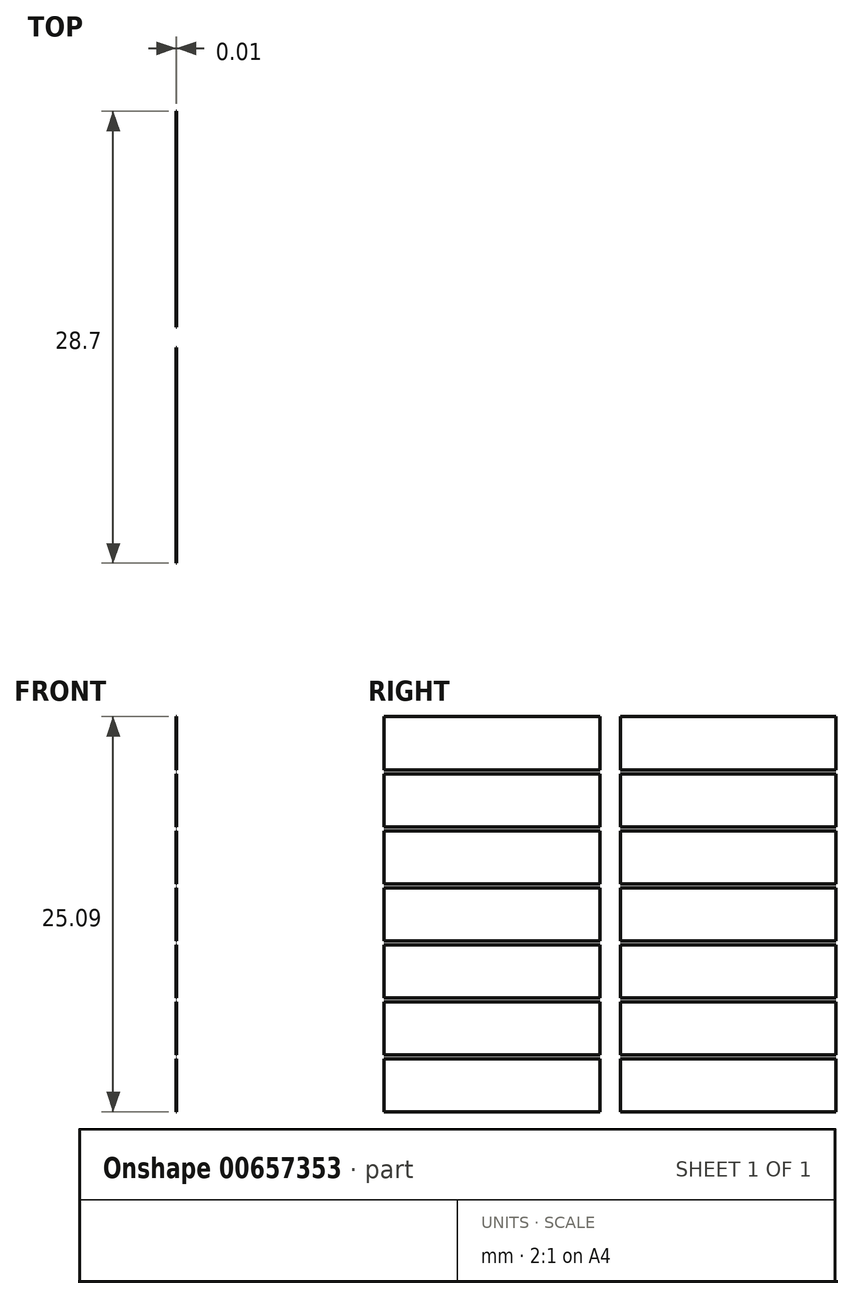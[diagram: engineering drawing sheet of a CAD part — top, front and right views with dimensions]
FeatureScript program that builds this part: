
annotation { "Feature Type Name" : "Feature", "Feature Type Description" : "" }
export const myFeature = defineFeature(function(context is Context, id is Id, definition is map)
    precondition{}
    {
        {
            var Q0;
            Q0=qCreatedBy(makeId("Right.planeOp"),FACE);
            var sketch = newSketch(context, id + "F0", { "sketchPlane" : qUnion([Q0])});
            skPoint(sketch, "E0.0", {"position": v(0, 0) * mm});
            skLineSegment(sketch, "E1.bottom", {"start": v(0, 0) * mm, "end": v(30, 0) * mm});
            skLineSegment(sketch, "E1.top", {"start": v(0, -30) * mm, "end": v(30, -30) * mm});
            skLineSegment(sketch, "E1.left", {"start": v(0, 0) * mm, "end": v(0, -30) * mm});
            skLineSegment(sketch, "E1.right", {"start": v(30, 0) * mm, "end": v(30, -30) * mm});
            skLineSegment(sketch, "E2.1", {"start": v(0.65, -0.65) * mm, "end": v(14.35, -0.65) * mm});
            skLineSegment(sketch, "E2.2", {"start": v(0.65, -0.65) * mm, "end": v(0.65, -2.2) * mm});
            skLineSegment(sketch, "E3", {"start": v(14.35, -2.2) * mm, "end": v(14.35, -0.65) * mm});
            skPoint(sketch, "E4.MirrorP", {"position": v(11.5, 0) * mm});
            skPoint(sketch, "E5.orphan", {"position": v(0, -26.74) * mm});
            skLineSegment(sketch, "E6", {"start": v(0.65, -2.46) * mm, "end": v(0.65, -4.02) * mm});
            skLineSegment(sketch, "E7", {"start": v(0.65, -4.02) * mm, "end": v(14.35, -4.02) * mm});
            skLineSegment(sketch, "E8", {"start": v(14.35, -4.02) * mm, "end": v(14.35, -2.46) * mm});
            skLineSegment(sketch, "E9.0", {"start": v(0.65, -4.27) * mm, "end": v(14.35, -4.27) * mm});
            skLineSegment(sketch, "E10", {"start": v(0.65, -4.27) * mm, "end": v(0.65, -5.83) * mm});
            skLineSegment(sketch, "E11", {"start": v(14.35, -5.83) * mm, "end": v(14.35, -4.27) * mm});
            skLineSegment(sketch, "E12.0", {"start": v(0.65, -7.64) * mm, "end": v(14.35, -7.64) * mm});
            skLineSegment(sketch, "E13", {"start": v(0.65, -6.08) * mm, "end": v(0.65, -7.64) * mm});
            skLineSegment(sketch, "E14", {"start": v(14.35, -6.08) * mm, "end": v(14.35, -7.64) * mm});
            skLineSegment(sketch, "E15.0", {"start": v(0.65, -7.9) * mm, "end": v(14.35, -7.9) * mm});
            skLineSegment(sketch, "E16", {"start": v(0.65, -7.9) * mm, "end": v(0.65, -9.45) * mm});
            skLineSegment(sketch, "E17", {"start": v(14.35, -9.45) * mm, "end": v(14.35, -7.9) * mm});
            skLineSegment(sketch, "E18.0", {"start": v(0.65, -11.26) * mm, "end": v(14.35, -11.26) * mm});
            skLineSegment(sketch, "E19", {"start": v(0.65, -9.7) * mm, "end": v(0.65, -11.26) * mm});
            skLineSegment(sketch, "E20", {"start": v(14.35, -9.7) * mm, "end": v(14.35, -11.26) * mm});
            skLineSegment(sketch, "E21.0", {"start": v(0.65, -11.51) * mm, "end": v(14.35, -11.51) * mm});
            skLineSegment(sketch, "E22", {"start": v(0.65, -11.51) * mm, "end": v(0.65, -13.07) * mm});
            skLineSegment(sketch, "E23", {"start": v(14.35, -13.07) * mm, "end": v(14.35, -11.51) * mm});
            skLineSegment(sketch, "E24.0", {"start": v(0.65, -14.88) * mm, "end": v(14.35, -14.88) * mm});
            skLineSegment(sketch, "E25", {"start": v(0.65, -13.32) * mm, "end": v(0.65, -14.88) * mm});
            skLineSegment(sketch, "E26", {"start": v(14.35, -14.88) * mm, "end": v(14.35, -13.32) * mm});
            skLineSegment(sketch, "E27.0", {"start": v(0.65, -15.13) * mm, "end": v(14.35, -15.13) * mm});
            skLineSegment(sketch, "E28", {"start": v(0.65, -15.13) * mm, "end": v(0.65, -16.7) * mm});
            skLineSegment(sketch, "E29", {"start": v(14.35, -16.7) * mm, "end": v(14.35, -15.13) * mm});
            skLineSegment(sketch, "E30.0", {"start": v(0.65, -18.5) * mm, "end": v(14.35, -18.5) * mm});
            skLineSegment(sketch, "E31", {"start": v(0.65, -16.7) * mm, "end": v(0.65, -18.5) * mm});
            skLineSegment(sketch, "E32", {"start": v(14.35, -18.5) * mm, "end": v(14.35, -16.94) * mm});
            skLineSegment(sketch, "E33.0", {"start": v(0.65, -18.75) * mm, "end": v(14.35, -18.75) * mm});
            skLineSegment(sketch, "E34", {"start": v(0.65, -18.75) * mm, "end": v(0.65, -20.31) * mm});
            skLineSegment(sketch, "E35", {"start": v(14.35, -18.75) * mm, "end": v(14.35, -20.31) * mm});
            skLineSegment(sketch, "E36.0", {"start": v(0.65, -22.12) * mm, "end": v(14.35, -22.12) * mm});
            skLineSegment(sketch, "E37", {"start": v(0.65, -20.56) * mm, "end": v(0.65, -22.12) * mm});
            skLineSegment(sketch, "E38", {"start": v(14.35, -20.56) * mm, "end": v(14.35, -22.12) * mm});
            skLineSegment(sketch, "E39.0", {"start": v(0.65, -22.37) * mm, "end": v(14.35, -22.37) * mm});
            skLineSegment(sketch, "E40", {"start": v(0.65, -22.37) * mm, "end": v(0.65, -23.93) * mm});
            skLineSegment(sketch, "E41", {"start": v(14.35, -22.37) * mm, "end": v(14.35, -23.93) * mm});
            skLineSegment(sketch, "E42.0", {"start": v(0.65, -25.74) * mm, "end": v(14.35, -25.74) * mm});
            skLineSegment(sketch, "E43", {"start": v(0.65, -24.18) * mm, "end": v(0.65, -25.74) * mm});
            skLineSegment(sketch, "E44", {"start": v(14.35, -24.18) * mm, "end": v(14.35, -25.74) * mm});
            skLineSegment(sketch, "E45", {"start": v(0.65, -2.46) * mm, "end": v(0.65, -2.2) * mm});
            skLineSegment(sketch, "E46", {"start": v(14.35, -2.46) * mm, "end": v(14.35, -2.2) * mm});
            skLineSegment(sketch, "E47", {"start": v(0.65, -6.08) * mm, "end": v(0.65, -5.83) * mm});
            skLineSegment(sketch, "E48", {"start": v(14.35, -6.08) * mm, "end": v(14.35, -5.83) * mm});
            skLineSegment(sketch, "E49", {"start": v(14.35, -24.18) * mm, "end": v(14.35, -23.93) * mm});
            skLineSegment(sketch, "E50", {"start": v(0.65, -24.18) * mm, "end": v(0.65, -23.93) * mm});
            skLineSegment(sketch, "E51", {"start": v(0.65, -20.56) * mm, "end": v(0.65, -20.31) * mm});
            skLineSegment(sketch, "E52", {"start": v(14.35, -20.56) * mm, "end": v(14.35, -20.31) * mm});
            skLineSegment(sketch, "E53", {"start": v(14.35, -16.94) * mm, "end": v(14.35, -16.7) * mm});
            skLineSegment(sketch, "E54", {"start": v(14.35, -13.32) * mm, "end": v(14.35, -13.07) * mm});
            skLineSegment(sketch, "E55", {"start": v(0.65, -13.32) * mm, "end": v(0.65, -13.07) * mm});
            skLineSegment(sketch, "E56", {"start": v(0.65, -9.7) * mm, "end": v(0.65, -9.45) * mm});
            skLineSegment(sketch, "E57", {"start": v(14.35, -9.7) * mm, "end": v(14.35, -9.45) * mm});
            skLineSegment(sketch, "E58.MirrorCS", {"start": v(29.35, -0.65) * mm, "end": v(29.35, -2.2) * mm});
            skLineSegment(sketch, "E59.MirrorCS", {"start": v(29.35, -2.46) * mm, "end": v(29.35, -2.2) * mm});
            skLineSegment(sketch, "E60.MirrorCS", {"start": v(29.35, -2.46) * mm, "end": v(29.35, -4.02) * mm});
            skLineSegment(sketch, "E61.MirrorCS", {"start": v(29.35, -20.56) * mm, "end": v(29.35, -22.12) * mm});
            skLineSegment(sketch, "E62.MirrorCS", {"start": v(15.65, -4.02) * mm, "end": v(15.65, -2.46) * mm});
            skLineSegment(sketch, "E63.MirrorCS", {"start": v(29.35, -20.56) * mm, "end": v(29.35, -20.31) * mm});
            skLineSegment(sketch, "E64.MirrorCS", {"start": v(29.35, -7.9) * mm, "end": v(29.35, -9.45) * mm});
            skLineSegment(sketch, "E65.MirrorCS", {"start": v(15.65, -16.7) * mm, "end": v(15.65, -15.13) * mm});
            skLineSegment(sketch, "E66.MirrorCS", {"start": v(29.35, -9.7) * mm, "end": v(29.35, -9.45) * mm});
            skLineSegment(sketch, "E67.MirrorCS", {"start": v(29.35, -6.08) * mm, "end": v(29.35, -5.83) * mm});
            skLineSegment(sketch, "E68.MirrorCS", {"start": v(15.65, -9.7) * mm, "end": v(15.65, -9.45) * mm});
            skLineSegment(sketch, "E69.MirrorCS", {"start": v(15.65, -22.37) * mm, "end": v(15.65, -23.93) * mm});
            skLineSegment(sketch, "E70.MirrorCS", {"start": v(29.35, -24.18) * mm, "end": v(29.35, -23.93) * mm});
            skLineSegment(sketch, "E71.MirrorCS", {"start": v(29.35, -4.27) * mm, "end": v(29.35, -5.83) * mm});
            skLineSegment(sketch, "E72.MirrorCS", {"start": v(15.65, -20.56) * mm, "end": v(15.65, -20.31) * mm});
            skLineSegment(sketch, "E73.MirrorCS", {"start": v(15.65, -9.45) * mm, "end": v(15.65, -7.9) * mm});
            skLineSegment(sketch, "E74.MirrorCS", {"start": v(29.35, -11.51) * mm, "end": v(29.35, -13.07) * mm});
            skLineSegment(sketch, "E75.MirrorCS", {"start": v(29.35, -13.32) * mm, "end": v(29.35, -13.07) * mm});
            skLineSegment(sketch, "E76.MirrorCS", {"start": v(15.65, -6.08) * mm, "end": v(15.65, -7.64) * mm});
            skLineSegment(sketch, "E77.MirrorCS", {"start": v(15.65, -14.88) * mm, "end": v(15.65, -13.32) * mm});
            skLineSegment(sketch, "E78.MirrorCS", {"start": v(29.35, -18.75) * mm, "end": v(29.35, -20.31) * mm});
            skLineSegment(sketch, "E79.MirrorCS", {"start": v(15.65, -24.18) * mm, "end": v(15.65, -23.93) * mm});
            skLineSegment(sketch, "E80.MirrorCS", {"start": v(29.35, -6.08) * mm, "end": v(29.35, -7.64) * mm});
            skLineSegment(sketch, "E81.MirrorCS", {"start": v(29.35, -13.32) * mm, "end": v(29.35, -14.88) * mm});
            skLineSegment(sketch, "E82.MirrorCS", {"start": v(15.65, -6.08) * mm, "end": v(15.65, -5.83) * mm});
            skLineSegment(sketch, "E83.MirrorCS", {"start": v(15.65, -18.5) * mm, "end": v(15.65, -16.94) * mm});
            skLineSegment(sketch, "E84.MirrorCS", {"start": v(29.35, -9.7) * mm, "end": v(29.35, -11.26) * mm});
            skLineSegment(sketch, "E85.MirrorCS", {"start": v(15.65, -13.07) * mm, "end": v(15.65, -11.51) * mm});
            skLineSegment(sketch, "E86.MirrorCS", {"start": v(15.65, -20.56) * mm, "end": v(15.65, -22.12) * mm});
            skLineSegment(sketch, "E87.MirrorCS", {"start": v(15.65, -13.32) * mm, "end": v(15.65, -13.07) * mm});
            skLineSegment(sketch, "E88.MirrorCS", {"start": v(15.65, -5.83) * mm, "end": v(15.65, -4.27) * mm});
            skLineSegment(sketch, "E89.MirrorCS", {"start": v(15.65, -9.7) * mm, "end": v(15.65, -11.26) * mm});
            skLineSegment(sketch, "E90.MirrorCS", {"start": v(29.35, -22.37) * mm, "end": v(29.35, -23.93) * mm});
            skLineSegment(sketch, "E91.MirrorCS", {"start": v(15.65, -18.75) * mm, "end": v(15.65, -20.31) * mm});
            skLineSegment(sketch, "E92.MirrorCS", {"start": v(29.35, -16.7) * mm, "end": v(29.35, -18.5) * mm});
            skLineSegment(sketch, "E93.MirrorCS", {"start": v(15.65, -2.2) * mm, "end": v(15.65, -0.65) * mm});
            skLineSegment(sketch, "E94.MirrorCS", {"start": v(29.35, -24.18) * mm, "end": v(29.35, -25.74) * mm});
            skLineSegment(sketch, "E95.MirrorCS", {"start": v(29.35, -15.13) * mm, "end": v(29.35, -16.7) * mm});
            skLineSegment(sketch, "E96.MirrorCS", {"start": v(15.65, -24.18) * mm, "end": v(15.65, -25.74) * mm});
            skLineSegment(sketch, "E97.MirrorCS", {"start": v(29.35, -4.02) * mm, "end": v(15.65, -4.02) * mm});
            skPoint(sketch, "E98.MirrorP", {"position": v(18.5, 0) * mm});
            skPoint(sketch, "E99.MirrorP", {"position": v(30, 0) * mm});
            skLineSegment(sketch, "E100.MirrorCS", {"start": v(29.35, -14.88) * mm, "end": v(15.65, -14.88) * mm});
            skLineSegment(sketch, "E101.MirrorCS", {"start": v(29.35, -0.65) * mm, "end": v(15.65, -0.65) * mm});
            skPoint(sketch, "E102.MirrorP", {"position": v(30, -26.74) * mm});
            skLineSegment(sketch, "E103.MirrorCS", {"start": v(29.35, -11.26) * mm, "end": v(15.65, -11.26) * mm});
            skLineSegment(sketch, "E104.MirrorCS", {"start": v(29.35, -18.75) * mm, "end": v(15.65, -18.75) * mm});
            skLineSegment(sketch, "E105.MirrorCS", {"start": v(29.35, -11.51) * mm, "end": v(15.65, -11.51) * mm});
            skLineSegment(sketch, "E106.MirrorCS", {"start": v(29.35, -22.37) * mm, "end": v(15.65, -22.37) * mm});
            skLineSegment(sketch, "E107.MirrorCS", {"start": v(29.35, -7.9) * mm, "end": v(15.65, -7.9) * mm});
            skLineSegment(sketch, "E108.MirrorCS", {"start": v(29.35, -25.74) * mm, "end": v(15.65, -25.74) * mm});
            skLineSegment(sketch, "E109.MirrorCS", {"start": v(29.35, -15.13) * mm, "end": v(15.65, -15.13) * mm});
            skLineSegment(sketch, "E110.MirrorCS", {"start": v(29.35, -4.27) * mm, "end": v(15.65, -4.27) * mm});
            skLineSegment(sketch, "E111.MirrorCS", {"start": v(29.35, -18.5) * mm, "end": v(15.65, -18.5) * mm});
            skLineSegment(sketch, "E112.MirrorCS", {"start": v(29.35, -7.64) * mm, "end": v(15.65, -7.64) * mm});
            skLineSegment(sketch, "E113.MirrorCS", {"start": v(29.35, -22.12) * mm, "end": v(15.65, -22.12) * mm});
            skLineSegment(sketch, "E114", {"start": v(15.65, -2.46) * mm, "end": v(15.65, -2.2) * mm});
            skLineSegment(sketch, "E115", {"start": v(15.65, -16.94) * mm, "end": v(15.65, -16.7) * mm});
            skSolve(sketch);
        }
        {
            var Q0;
            Q0=makeQuery(id+"F0.imprint","IMPRINT",FACE,{"disambiguationData":[TD([[makeQuery(id+"F0.imprint","IMPRINT",EDGE,{"derivedFrom":sQuery(id+"F0.wireOp",EDGE,"14657d91-79c0-4d6f-9dc8-bfef05761bba.0")}),1.0]])]});
            var Q1;
            Q1=makeQuery(id+"F0.imprint","IMPRINT",FACE,{"disambiguationData":[TD([[makeQuery(id+"F0.imprint","IMPRINT",EDGE,{"derivedFrom":sQuery(id+"F0.wireOp",EDGE,"d10a1318-4c6c-4e2f-b301-627ccdfaac9c.0")}),1.0]])]});
            var Q2;
            Q2=makeQuery(id+"F0.imprint","IMPRINT",FACE,{"disambiguationData":[TD([[makeQuery(id+"F0.imprint","IMPRINT",EDGE,{"derivedFrom":sQuery(id+"F0.wireOp",EDGE,"34b941e1-9213-4a0b-9b3c-3fd5b53a19226.MirrorCS")}),1.0]])]});
            var Q3;
            Q3=makeQuery(id+"F0.imprint","IMPRINT",FACE,{"disambiguationData":[TD([[makeQuery(id+"F0.imprint","IMPRINT",EDGE,{"derivedFrom":sQuery(id+"F0.wireOp",EDGE,"e52c6cc0-2e10-4916-a505-43da0128bf07.0")}),-1.0]])]});
            var Q4;
            Q4=makeQuery(id+"F0.imprint","IMPRINT",FACE,{"disambiguationData":[TD([[makeQuery(id+"F0.imprint","IMPRINT",EDGE,{"derivedFrom":sQuery(id+"F0.wireOp",EDGE,"34b941e1-9213-4a0b-9b3c-3fd5b53a19229.MirrorCS")}),1.0]])]});
            var Q5;
            Q5=makeQuery(id+"F0.imprint","IMPRINT",FACE,{"disambiguationData":[TD([[makeQuery(id+"F0.imprint","IMPRINT",EDGE,{"derivedFrom":sQuery(id+"F0.wireOp",EDGE,"34b941e1-9213-4a0b-9b3c-3fd5b53a19223.MirrorCS")}),1.0]])]});
            var Q6;
            Q6=makeQuery(id+"F0.imprint","IMPRINT",FACE,{"disambiguationData":[TD([[makeQuery(id+"F0.imprint","IMPRINT",EDGE,{"derivedFrom":sQuery(id+"F0.wireOp",EDGE,"E2.1")}),-1.0]])]});
            var Q7;
            Q7=makeQuery(id+"F0.imprint","IMPRINT",FACE,{"disambiguationData":[TD([[makeQuery(id+"F0.imprint","IMPRINT",EDGE,{"derivedFrom":sQuery(id+"F0.wireOp",EDGE,"34b941e1-9213-4a0b-9b3c-3fd5b53a19222.MirrorCS")}),1.0]])]});
            var Q8;
            Q8=makeQuery(id+"F0.imprint","IMPRINT",FACE,{"disambiguationData":[TD([[makeQuery(id+"F0.imprint","IMPRINT",EDGE,{"derivedFrom":sQuery(id+"F0.wireOp",EDGE,"34b941e1-9213-4a0b-9b3c-3fd5b53a19224.MirrorCS")}),1.0]])]});
            var Q9;
            Q9=makeQuery(id+"F0.imprint","IMPRINT",FACE,{"disambiguationData":[TD([[makeQuery(id+"F0.imprint","IMPRINT",EDGE,{"derivedFrom":sQuery(id+"F0.wireOp",EDGE,"34b941e1-9213-4a0b-9b3c-3fd5b53a19221.MirrorCS")}),-1.0]])]});
            var Q10;
            Q10=makeQuery(id+"F0.imprint","IMPRINT",FACE,{"disambiguationData":[TD([[makeQuery(id+"F0.imprint","IMPRINT",EDGE,{"derivedFrom":sQuery(id+"F0.wireOp",EDGE,"7f593fd2-97bd-4d00-b395-f38d8aa9202c.0")}),1.0]])]});
            var Q11;
            Q11=makeQuery(id+"F0.imprint","IMPRINT",FACE,{"disambiguationData":[TD([[makeQuery(id+"F0.imprint","IMPRINT",EDGE,{"derivedFrom":sQuery(id+"F0.wireOp",EDGE,"7881708b-2482-4012-b24c-5590632c987f.0")}),1.0]])]});
            var Q12;
            Q12=makeQuery(id+"F0.imprint","IMPRINT",FACE,{"disambiguationData":[TD([[makeQuery(id+"F0.imprint","IMPRINT",EDGE,{"derivedFrom":sQuery(id+"F0.wireOp",EDGE,"b2c296a6-979c-4eb4-8951-c574cebceffd.0")}),1.0]])]});
            var Q13;
            Q13=makeQuery(id+"F0.imprint","IMPRINT",FACE,{"disambiguationData":[TD([[makeQuery(id+"F0.imprint","IMPRINT",EDGE,{"derivedFrom":sQuery(id+"F0.wireOp",EDGE,"E2.0")}),-1.0]])]});
            var Q14;
            Q14=makeQuery(id+"F0.imprint","IMPRINT",FACE,{"disambiguationData":[TD([[makeQuery(id+"F0.imprint","IMPRINT",EDGE,{"derivedFrom":sQuery(id+"F0.wireOp",EDGE,"E9.0")}),-1.0]])]});
            var Q15;
            Q15=makeQuery(id+"F0.imprint","IMPRINT",FACE,{"disambiguationData":[TD([[makeQuery(id+"F0.imprint","IMPRINT",EDGE,{"derivedFrom":sQuery(id+"F0.wireOp",EDGE,"E21.0")}),-1.0]])]});
            var Q16;
            Q16=makeQuery(id+"F0.imprint","IMPRINT",FACE,{"disambiguationData":[TD([[makeQuery(id+"F0.imprint","IMPRINT",EDGE,{"derivedFrom":sQuery(id+"F0.wireOp",EDGE,"E15.0")}),-1.0]])]});
            var Q17;
            Q17=makeQuery(id+"F0.imprint","IMPRINT",FACE,{"disambiguationData":[TD([[makeQuery(id+"F0.imprint","IMPRINT",EDGE,{"derivedFrom":sQuery(id+"F0.wireOp",EDGE,"E27.0")}),-1.0]])]});
            var Q18;
            Q18=makeQuery(id+"F0.imprint","IMPRINT",FACE,{"disambiguationData":[TD([[makeQuery(id+"F0.imprint","IMPRINT",EDGE,{"derivedFrom":sQuery(id+"F0.wireOp",EDGE,"E33.0")}),-1.0]])]});
            var Q19;
            Q19=makeQuery(id+"F0.imprint","IMPRINT",FACE,{"disambiguationData":[TD([[makeQuery(id+"F0.imprint","IMPRINT",EDGE,{"derivedFrom":sQuery(id+"F0.wireOp",EDGE,"E39.0")}),-1.0]])]});
            var Q20;
            Q20=makeQuery(id+"F0.imprint","IMPRINT",FACE,{"disambiguationData":[TD([[makeQuery(id+"F0.imprint","IMPRINT",EDGE,{"derivedFrom":sQuery(id+"F0.wireOp",EDGE,"E69.MirrorCS")}),1.0]])]});
            var Q21;
            Q21=makeQuery(id+"F0.imprint","IMPRINT",FACE,{"disambiguationData":[TD([[makeQuery(id+"F0.imprint","IMPRINT",EDGE,{"derivedFrom":sQuery(id+"F0.wireOp",EDGE,"E67.MirrorCS")}),1.0]])]});
            var Q22;
            Q22=makeQuery(id+"F0.imprint","IMPRINT",FACE,{"disambiguationData":[TD([[makeQuery(id+"F0.imprint","IMPRINT",EDGE,{"derivedFrom":sQuery(id+"F0.wireOp",EDGE,"E64.MirrorCS")}),-1.0]])]});
            var Q23;
            Q23=makeQuery(id+"F0.imprint","IMPRINT",FACE,{"disambiguationData":[TD([[makeQuery(id+"F0.imprint","IMPRINT",EDGE,{"derivedFrom":sQuery(id+"F0.wireOp",EDGE,"E74.MirrorCS")}),-1.0]])]});
            var Q24;
            Q24=makeQuery(id+"F0.imprint","IMPRINT",FACE,{"disambiguationData":[TD([[makeQuery(id+"F0.imprint","IMPRINT",EDGE,{"derivedFrom":sQuery(id+"F0.wireOp",EDGE,"E61.MirrorCS")}),-1.0]])]});
            var Q25;
            Q25=makeQuery(id+"F0.imprint","IMPRINT",FACE,{"disambiguationData":[TD([[makeQuery(id+"F0.imprint","IMPRINT",EDGE,{"derivedFrom":sQuery(id+"F0.wireOp",EDGE,"E65.MirrorCS")}),-1.0]])]});
            var Q26;
            Q26=makeQuery(id+"F0.imprint","IMPRINT",FACE,{"disambiguationData":[TD([[makeQuery(id+"F0.imprint","IMPRINT",EDGE,{"derivedFrom":sQuery(id+"F0.wireOp",EDGE,"E59.MirrorCS")}),1.0]])]});
            var Q27;
            Q27=makeQuery(id+"F0.imprint","IMPRINT",FACE,{"disambiguationData":[TD([[makeQuery(id+"F0.imprint","IMPRINT",EDGE,{"derivedFrom":sQuery(id+"F0.wireOp",EDGE,"bab827ae-1c97-406d-a0ac-fc6b01f04ac5.0")}),-1.0]])]});
            extrude(context, id + "F1", {"entities" : qUnion([Q0, Q1, Q2, Q3, Q4, Q5, Q6, Q7, Q8, Q9, Q10, Q11, Q12, Q13, Q14, Q15, Q16, Q17, Q18, Q19, Q20, Q21, Q22, Q23, Q24, Q25, Q26, Q27]), "depth" : 0.01 * mm, "offsetDistance" : 25 * mm});
        }
    });
